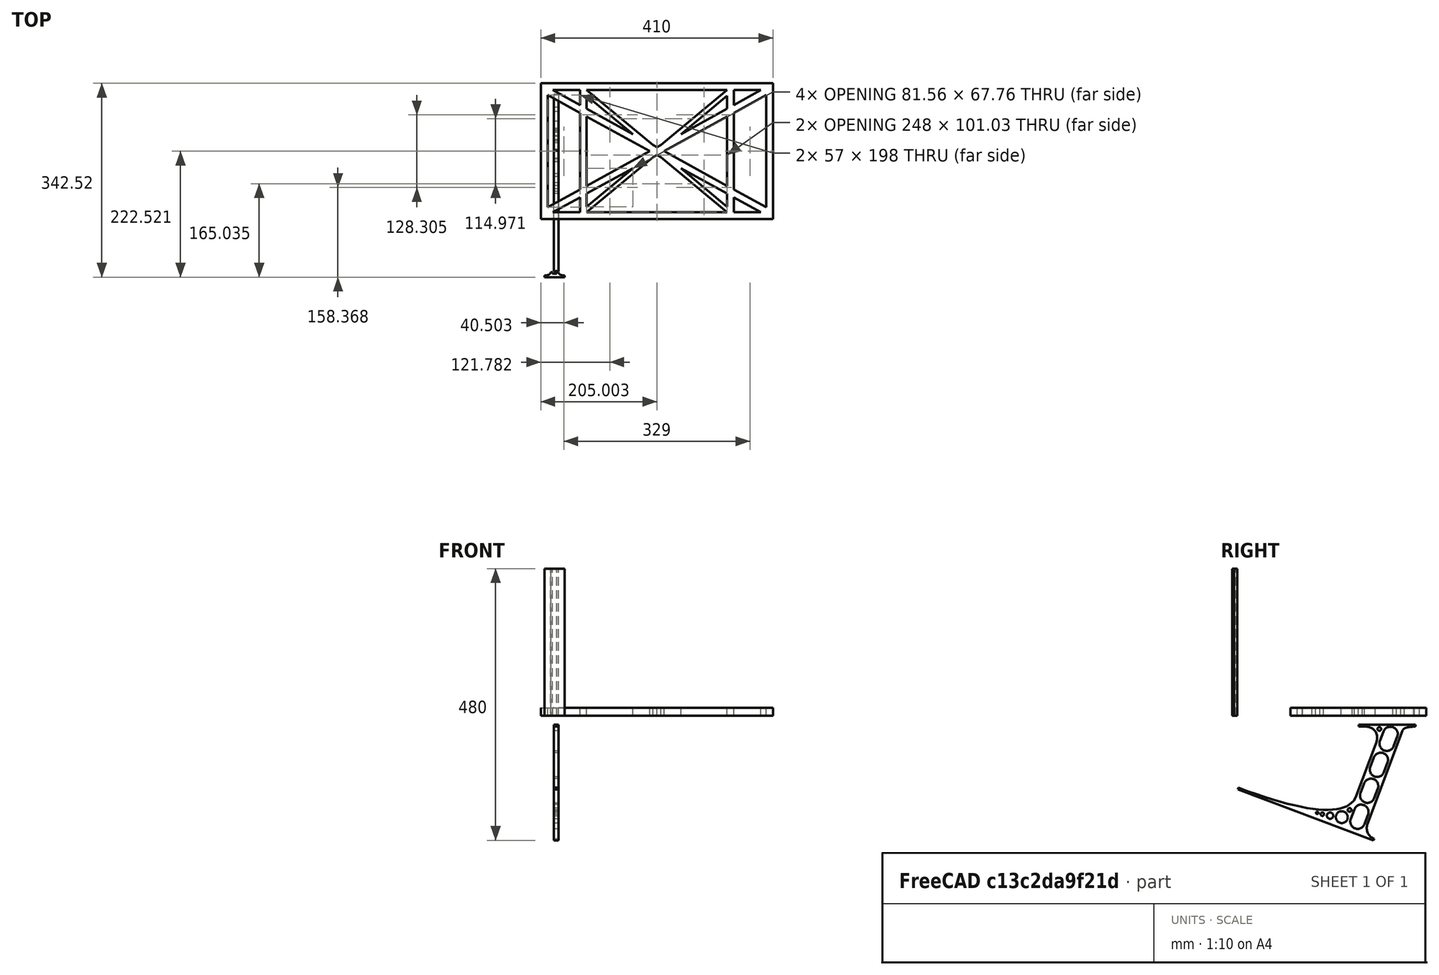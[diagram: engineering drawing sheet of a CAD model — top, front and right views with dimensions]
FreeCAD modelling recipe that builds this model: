
FCSTD DOCUMENT  (FreeCAD 0.19R0.19.2)
Label: laptopStand050
License: All rights reserved
LicenseURL: http://en.wikipedia.org/wiki/All_rights_reserved
objects: Sketcher::SketchObject×3, Part::Extrusion×3
note: 6 computed .brp shape members not serialized (recipe doc carries the construction recipe); baked Part::Feature solids carry a one-line shape summary decoded from their .brp

FEATURE [Sketcher::SketchObject] Sketch
  FullyConstrained = false
  sketch-geometry (72):
    g0: LineSegment StartX=-22.9272 StartY=136.221 StartZ=0 EndX=387.073 EndY=136.221 EndZ=0
    g1: LineSegment StartX=-22.9272 StartY=-103.779 StartZ=0 EndX=387.073 EndY=-103.779 EndZ=0
    g2: LineSegment StartX=375.073 StartY=115.221 StartZ=0 EndX=318.073 EndY=83.9235 EndZ=0
    g3: LineSegment StartX=-10.9272 StartY=-82.7794 StartZ=0 EndX=46.0728 EndY=-51.4823 EndZ=0
    g4: LineSegment StartX=-1.92719 StartY=124.221 StartZ=0 EndX=46.0728 EndY=97.8651 EndZ=0
    g5: LineSegment StartX=366.073 StartY=-91.7794 StartZ=0 EndX=318.073 EndY=-65.424 EndZ=0
    g6: LineSegment StartX=-10.9272 StartY=115.221 StartZ=0 EndX=-10.9272 EndY=-82.7794 EndZ=0
    g7: LineSegment StartX=375.073 StartY=-82.7794 StartZ=0 EndX=375.073 EndY=115.221 EndZ=0
    g8: LineSegment StartX=-1.92719 StartY=-91.7794 StartZ=0 EndX=46.0728 EndY=-91.7794 EndZ=0
    g9: LineSegment StartX=318.073 StartY=124.221 StartZ=0 EndX=366.073 EndY=124.221 EndZ=0
    g10: LineSegment StartX=306.073 StartY=-81.8102 StartZ=0 EndX=224.513 EndY=-14.0532 EndZ=0
    g11: LineSegment StartX=58.0728 StartY=114.251 StartZ=0 EndX=139.632 EndY=46.4944 EndZ=0
    g12: LineSegment StartX=306.073 StartY=124.221 StartZ=0 EndX=189.124 EndY=27.0628 EndZ=0
    g13: LineSegment StartX=58.0728 StartY=-91.7794 StartZ=0 EndX=175.022 EndY=5.37834 EndZ=0
    g14: LineSegment StartX=46.0728 StartY=124.221 StartZ=0 EndX=46.0728 EndY=97.8651 EndZ=0
    g15: LineSegment StartX=58.0728 StartY=-81.8102 StartZ=0 EndX=58.0728 EndY=-58.8351 EndZ=0
    g16: LineSegment StartX=318.073 StartY=124.221 StartZ=0 EndX=318.073 EndY=97.8651 EndZ=0
    g17: LineSegment StartX=306.073 StartY=114.251 StartZ=0 EndX=306.073 EndY=91.2763 EndZ=0
    g18: LineSegment StartX=224.513 StartY=46.4944 StartZ=0 EndX=306.073 EndY=114.251 EndZ=0
    g19: LineSegment StartX=175.022 StartY=27.0628 StartZ=0 EndX=58.0728 EndY=124.221 EndZ=0
    g20: LineSegment StartX=169.377 StartY=16.2206 StartZ=0 EndX=58.0728 EndY=77.3346 EndZ=0
    g21: LineSegment StartX=139.632 StartY=-14.0532 StartZ=0 EndX=58.0728 EndY=-81.8102 EndZ=0
    g22: LineSegment StartX=194.768 StartY=16.2206 StartZ=0 EndX=306.073 EndY=-44.8935 EndZ=0
    g23: LineSegment StartX=224.513 StartY=46.4944 StartZ=0 EndX=306.073 EndY=91.2763 EndZ=0
    g24: LineSegment StartX=175.022 StartY=27.0628 StartZ=0 EndX=179.022 EndY=24.8665 EndZ=0
    g25: LineSegment StartX=139.632 StartY=-14.0532 StartZ=0 EndX=58.0728 EndY=-58.8351 EndZ=0
    g26: LineSegment StartX=189.124 StartY=5.37834 StartZ=0 EndX=185.124 EndY=7.57463 EndZ=0
    g27: LineSegment StartX=189.124 StartY=5.37834 StartZ=0 EndX=306.073 EndY=-91.7794 EndZ=0
    g28: LineSegment StartX=306.073 StartY=77.3346 StartZ=0 EndX=306.073 EndY=-44.8935 EndZ=0
    g29: LineSegment StartX=318.073 StartY=83.9235 StartZ=0 EndX=318.073 EndY=-51.4823 EndZ=0
    g30: LineSegment StartX=318.073 StartY=97.8651 StartZ=0 EndX=366.073 EndY=124.221 EndZ=0
    g31: LineSegment StartX=306.073 StartY=77.3346 StartZ=0 EndX=194.768 EndY=16.2206 EndZ=0
    g32: LineSegment StartX=306.073 StartY=-58.8351 StartZ=0 EndX=224.513 EndY=-14.0532 EndZ=0
    g33: LineSegment StartX=306.073 StartY=-58.8351 StartZ=0 EndX=306.073 EndY=-81.8102 EndZ=0
    g34: LineSegment StartX=318.073 StartY=-51.4823 StartZ=0 EndX=375.073 EndY=-82.7794 EndZ=0
    g35: LineSegment StartX=318.073 StartY=-65.424 StartZ=0 EndX=318.073 EndY=-91.7794 EndZ=0
    g36: LineSegment StartX=318.073 StartY=-91.7794 StartZ=0 EndX=366.073 EndY=-91.7794 EndZ=0
    g37: LineSegment StartX=58.0728 StartY=-44.8935 StartZ=0 EndX=58.0728 EndY=77.3346 EndZ=0
    g38: LineSegment StartX=46.0728 StartY=-65.424 StartZ=0 EndX=-1.92719 EndY=-91.7794 EndZ=0
    g39: LineSegment StartX=46.0728 StartY=-65.424 StartZ=0 EndX=46.0728 EndY=-91.7794 EndZ=0
    g40: LineSegment StartX=58.0728 StartY=-44.8935 StartZ=0 EndX=169.377 EndY=16.2206 EndZ=0
    g41: LineSegment StartX=58.0728 StartY=91.2763 StartZ=0 EndX=58.0728 EndY=114.251 EndZ=0
    g42: LineSegment StartX=46.0728 StartY=83.9235 StartZ=0 EndX=46.0728 EndY=-51.4823 EndZ=0
    g43: LineSegment StartX=46.0728 StartY=124.221 StartZ=0 EndX=-1.92719 EndY=124.221 EndZ=0
    g44: LineSegment StartX=58.0728 StartY=91.2763 StartZ=0 EndX=139.632 EndY=46.4944 EndZ=0
    g45: LineSegment StartX=46.0728 StartY=83.9235 StartZ=0 EndX=-10.9272 EndY=115.221 EndZ=0
    g46: LineSegment StartX=-22.9272 StartY=136.221 StartZ=0 EndX=-42.9272 EndY=136.221 EndZ=0
    g47: LineSegment StartX=387.073 StartY=136.221 StartZ=0 EndX=407.073 EndY=136.221 EndZ=0
    g48: LineSegment StartX=-42.9272 StartY=136.221 StartZ=0 EndX=-42.9272 EndY=-103.779 EndZ=0
    g49: LineSegment StartX=-22.9272 StartY=-103.779 StartZ=0 EndX=-42.9272 EndY=-103.779 EndZ=0
    g50: LineSegment StartX=407.073 StartY=136.221 StartZ=0 EndX=407.073 EndY=-103.779 EndZ=0
    g51: LineSegment StartX=387.073 StartY=-103.779 StartZ=0 EndX=407.073 EndY=-103.779 EndZ=0
    g52: LineSegment StartX=179.022 StartY=27.0628 StartZ=0 EndX=179.022 EndY=124.221 EndZ=0
    g53: LineSegment StartX=185.124 StartY=27.0628 StartZ=0 EndX=185.124 EndY=124.221 EndZ=0
    g54: LineSegment StartX=179.022 StartY=27.0628 StartZ=0 EndX=179.022 EndY=24.8665 EndZ=0
    g55: LineSegment StartX=185.124 StartY=27.0628 StartZ=0 EndX=185.124 EndY=24.8665 EndZ=0
    g56: LineSegment StartX=185.124 StartY=7.57463 StartZ=0 EndX=185.124 EndY=-91.7794 EndZ=0
    g57: LineSegment StartX=179.022 StartY=7.57463 StartZ=0 EndX=179.022 EndY=-91.7794 EndZ=0
    g58: LineSegment StartX=189.124 StartY=27.0628 StartZ=0 EndX=185.124 EndY=24.8665 EndZ=0
    g59: LineSegment StartX=175.022 StartY=5.37834 StartZ=0 EndX=179.022 EndY=7.57463 EndZ=0
    g60: ArcOfCircle CenterX=-26.9272 CenterY=22.1087 CenterZ=0 NormalX=0 NormalY=0 NormalZ=1 AngleXU=0 Radius=8 StartAngle=1e-16 EndAngle=3.14159
    g61: ArcOfCircle CenterX=-26.9272 CenterY=-83.7794 CenterZ=0 NormalX=0 NormalY=0 NormalZ=1 AngleXU=0 Radius=8 StartAngle=3.14159 EndAngle=6.28319
    g62: LineSegment StartX=-34.9272 StartY=22.1087 StartZ=0 EndX=-34.9272 EndY=-83.7794 EndZ=0
    g63: LineSegment StartX=-18.9272 StartY=22.1087 StartZ=0 EndX=-18.9272 EndY=-83.7794 EndZ=0
    g64: LineSegment StartX=185.124 StartY=-91.7794 StartZ=0 EndX=306.073 EndY=-91.7794 EndZ=0
    g65: LineSegment StartX=179.022 StartY=-91.7794 StartZ=0 EndX=58.0728 EndY=-91.7794 EndZ=0
    g66: LineSegment StartX=306.073 StartY=124.221 StartZ=0 EndX=185.124 EndY=124.221 EndZ=0
    g67: LineSegment StartX=179.022 StartY=124.221 StartZ=0 EndX=58.0728 EndY=124.221 EndZ=0
    g68: ArcOfCircle CenterX=391.073 CenterY=22.1087 CenterZ=0 NormalX=0 NormalY=0 NormalZ=1 AngleXU=0 Radius=8 StartAngle=-4.4e-15 EndAngle=3.14159
    g69: LineSegment StartX=399.073 StartY=22.1087 StartZ=0 EndX=399.073 EndY=-83.7794 EndZ=0
    g70: LineSegment StartX=383.073 StartY=22.1087 StartZ=0 EndX=383.073 EndY=-83.7794 EndZ=0
    g71: ArcOfCircle CenterX=391.073 CenterY=-83.7794 CenterZ=0 NormalX=0 NormalY=0 NormalZ=1 AngleXU=0 Radius=8 StartAngle=3.14159 EndAngle=6.28319
  constraints (146):
    c: Horizontal(g0)
    c: Distance(g0) = 410
    c: Horizontal(g1)
    c: Block(g0)
    c: Horizontal(g8)
    c: Horizontal(g9)
    c: Tangent(g5,g20)
    c: PointOnObject(g20,g3)
    c: PointOnObject(g22,g2)
    c: Coincident(g44,g11)
    c: Coincident(g24,g19)
    c: Coincident(g18,g23)
    c: Coincident(g25,g21)
    c: Coincident(g32,g10)
    c: Coincident(g27,g26)
    c: Coincident(g18,g17)
    c: Tangent(g17,g28)
    c: Tangent(g16,g29)
    c: Coincident(g23,g17)
    c: Tangent(g23,g30)
    c: Coincident(g2,g29)
    c: Coincident(g31,g28)
    c: Tangent(g2,g31)
    c: Coincident(g33,g10)
    c: Tangent(g5,g32)
    c: Tangent(g28,g33)
    c: Coincident(g22,g28)
    c: Tangent(g22,g34)
    c: Coincident(g29,g34)
    c: Coincident(g35,g5)
    c: Tangent(g29,g35)
    c: Coincident(g21,g15)
    c: Tangent(g15,g37)
    c: Coincident(g25,g15)
    c: Tangent(g25,g38)
    c: Coincident(g39,g38)
    c: Tangent(g14,g39)
    c: Coincident(g3,g42)
    c: Coincident(g40,g37)
    c: Tangent(g3,g40)
    c: Tangent(g37,g41)
    c: Tangent(g14,g42)
    c: Coincident(g11,g41)
    c: Coincident(g4,g14)
    c: Coincident(g44,g41)
    c: Tangent(g4,g44)
    c: Coincident(g20,g37)
    c: Coincident(g45,g42)
    c: Tangent(g20,g45)
    c: Block(g19)
    c: Block(g12)
    c: Block(g16)
    c: Block(g30)
    c: Block(g2)
    c: Block(g34)
    c: Block(g7)
    c: Block(g32)
    c: Block(g33)
    c: Block(g5)
    c: Block(g35)
    c: Block(g18)
    c: Block(g27)
    c: Block(g13)
    c: Block(g25)
    c: Block(g21)
    c: Block(g39)
    c: Block(g38)
    c: Block(g3)
    c: Block(g6)
    c: Block(g45)
    c: Block(g4)
    c: Block(g14)
    c: Block(g11)
    c: Block(g41)
    c: Block(g31)
    c: Block(g28)
    c: Block(g20)
    c: Block(g40)
    c: Block(g43)
    c: Block(g9)
    c: Block(g36)
    c: Block(g8)
    c: Horizontal(g46)
    c: Distance(g46) = 20
    c: Coincident(g47,g0)
    c: Horizontal(g47)
    c: Distance(g47) = 20
    c: Coincident(g48,g46)
    c: Vertical(g48)
    c: Horizontal(g49)
    c: Coincident(g49,g48)
    c: Coincident(g50,g47)
    c: Vertical(g50)
    c: Coincident(g51,g1)
    c: Horizontal(g51)
    c: Coincident(g51,g50)
    c: Block(g50)
    c: Block(g49)
    c: Block(g48)
    c: Block(g1)
    c: Vertical(g52)
    c: Vertical(g53)
    c: Vertical(g54)
    c: Vertical(g55)
    c: Tangent(g55,g56)
    c: Tangent(g54,g57)
    c: Coincident(g24,g54)
    c: Coincident(g26,g56)
    c: Block(g52)
    c: Block(g53)
    c: Block(g57)
    c: Block(g56)
    c: Coincident(g58,g12)
    c: Coincident(g58,g55)
    c: Coincident(g59,g13)
    c: Coincident(g59,g57)
    c: Tangent(g60,g63) = 1.5708
    c: Tangent(g60,g62) = -1.5708
    c: Tangent(g62,g61) = -1.5708
    c: Tangent(g63,g61) = 1.5708
    c: Vertical(g62)
    c: Equal(g60,g61)
    c: Block(g63)
    c: Block(g62)
    c: Coincident(g64,g56)
    c: Coincident(g64,g27)
    c: Horizontal(g64)
    c: Coincident(g65,g57)
    c: Coincident(g65,g13)
    c: Horizontal(g65)
    c: Coincident(g66,g12)
    c: Coincident(g66,g53)
    c: Horizontal(g66)
    c: Coincident(g67,g52)
    c: Coincident(g67,g19)
    c: Horizontal(g67)
    c: Distance(g51) = 20
    c: Distance(g1) = 410
    c: Tangent(g68,g69) = 1.5708
    c: Tangent(g69,g71) = 1.5708
    c: Equal(g68,g71)
    c: Coincident(g70,g68)
    c: Coincident(g70,g71)
    c: Vertical(g70)
    c: Block(g69)
    c: Block(g70)
FEATURE [Sketcher::SketchObject] Sketch001
  FullyConstrained = true
  MapMode = 4
  Placement = pos=(0,0,0) rot=(0.57735,0.57735,0.57735;2.0944rad)
  Support = -> [Sketch]
  sketch-geometry (46):
    g0: BSplineCurve PolesCount=3 KnotsCount=2 Degree=2 IsPeriodic=0
    g1: ArcOfCircle CenterX=73.122 CenterY=-32.2909 CenterZ=0 NormalX=0 NormalY=0 NormalZ=1 AngleXU=0 Radius=13 StartAngle=5.92268 EndAngle=9.06428
    g2: ArcOfCircle CenterX=66.7816 CenterY=-49.1439 CenterZ=0 NormalX=0 NormalY=0 NormalZ=1 AngleXU=0 Radius=13 StartAngle=2.78068 EndAngle=5.92131
    g3: ArcOfCircle CenterX=55.9263 CenterY=-78.1807 CenterZ=0 NormalX=0 NormalY=0 NormalZ=1 AngleXU=0 Radius=13 StartAngle=5.92268 EndAngle=9.06428
    g4: ArcOfCircle CenterX=49.5884 CenterY=-95.0342 CenterZ=0 NormalX=0 NormalY=0 NormalZ=1 AngleXU=0 Radius=13 StartAngle=2.78068 EndAngle=5.92131
    g5: ArcOfCircle CenterX=38.7206 CenterY=-124.067 CenterZ=0 NormalX=0 NormalY=0 NormalZ=1 AngleXU=0 Radius=13 StartAngle=5.92268 EndAngle=9.06428
    g6: ArcOfCircle CenterX=32.3875 CenterY=-140.92 CenterZ=0 NormalX=0 NormalY=0 NormalZ=1 AngleXU=0 Radius=13 StartAngle=2.78068 EndAngle=5.92131
    g7: ArcOfCircle CenterX=21.4715 CenterY=-169.934 CenterZ=0 NormalX=0 NormalY=0 NormalZ=1 AngleXU=0 Radius=13 StartAngle=5.92268 EndAngle=9.06428
    g8: ArcOfCircle CenterX=15.1336 CenterY=-186.787 CenterZ=0 NormalX=0 NormalY=0 NormalZ=1 AngleXU=0 Radius=13 StartAngle=2.78068 EndAngle=5.92131
    g9-g12: Circle x4 (B-spline internal-alignment scaffolding for g13; pole/knot coordinates omitted)
    g13: BSplineCurve PolesCount=4 KnotsCount=2 Degree=3 IsPeriodic=0
    g14: GeomPoint X=28.8094 Y=-19.0875 Z=0
    g15: GeomPoint X=47.0443 Y=-50.4712 Z=0
    g16: Circle CenterX=53.5586 CenterY=-23.2695 CenterZ=0 NormalX=0 NormalY=0 NormalZ=1 AngleXU=0 Radius=3.24518
    g17: Circle CenterX=-195.441 CenterY=-127.082 CenterZ=0 NormalX=0 NormalY=0 NormalZ=1 AngleXU=0 Radius=1
    g18: Circle CenterX=-8.24091 CenterY=-197.481 CenterZ=0 NormalX=0 NormalY=0 NormalZ=1 AngleXU=0 Radius=1
    g19: Circle CenterX=12.8789 CenterY=-141.321 CenterZ=0 NormalX=0 NormalY=0 NormalZ=1 AngleXU=0 Radius=1
    g20: BSplineCurve PolesCount=3 KnotsCount=2 Degree=2 IsPeriodic=0
    g21: GeomPoint X=-195.441 Y=-127.082 Z=0
    g22: GeomPoint X=12.8789 Y=-141.321 Z=0
    g23: Circle CenterX=-12.8016 CenterY=-179.036 CenterZ=0 NormalX=0 NormalY=0 NormalZ=1 AngleXU=0 Radius=10.5072
    g24: Circle CenterX=0.933922 CenterY=-166.43 CenterZ=0 NormalX=0 NormalY=0 NormalZ=1 AngleXU=0 Radius=3.26661
    g25: Circle CenterX=-33.5518 CenterY=-176.44 CenterZ=0 NormalX=0 NormalY=0 NormalZ=1 AngleXU=0 Radius=5.64388
    g26: Circle CenterX=-47.2366 CenterY=-173.859 CenterZ=0 NormalX=0 NormalY=0 NormalZ=1 AngleXU=0 Radius=3.01653
    g27: Circle CenterX=-56.2595 CenterY=-171.456 CenterZ=0 NormalX=0 NormalY=0 NormalZ=1 AngleXU=0 Radius=2.12826
    g28: ArcOfCircle CenterX=51.2151 CenterY=-198.473 CenterZ=0 NormalX=0 NormalY=0 NormalZ=1 AngleXU=0 Radius=20 StartAngle=2.78189 EndAngle=4.35269
    g29: LineSegment StartX=32.4951 StartY=-191.433 StartZ=0 EndX=94.6577 EndY=-26.1351 EndZ=0
    g30: LineSegment StartX=43.1192 StartY=-220.001 StartZ=0 EndX=-196.497 EndY=-129.89 EndZ=0
    g31: LineSegment StartX=43.1192 StartY=-220.001 StartZ=0 EndX=44.1752 EndY=-217.193 EndZ=0
    g32: LineSegment StartX=117.223 StartY=-19.0875 StartZ=0 EndX=117.223 EndY=-16.0875 EndZ=0
    g33: LineSegment StartX=117.223 StartY=-16.0875 StartZ=0 EndX=17.2232 EndY=-16.0875 EndZ=0
    g34: LineSegment StartX=17.2232 StartY=-16.0875 StartZ=0 EndX=17.2232 EndY=-19.0875 EndZ=0
    g35: LineSegment StartX=28.8094 StartY=-19.0875 StartZ=0 EndX=17.2232 EndY=-19.0875 EndZ=0
    g36: LineSegment StartX=47.0443 StartY=-50.4712 StartZ=0 EndX=12.8789 EndY=-141.321 EndZ=0
    g37: LineSegment StartX=-195.441 StartY=-127.082 StartZ=0 EndX=-196.497 EndY=-129.89 EndZ=0
    g38: LineSegment StartX=85.2864 StartY=-36.8765 StartZ=0 EndX=78.9396 EndY=-53.7463 EndZ=0
    g39: LineSegment StartX=60.9577 StartY=-27.7052 StartZ=0 EndX=54.6191 EndY=-44.5532 EndZ=0
    g40: LineSegment StartX=68.0907 StartY=-82.7664 StartZ=0 EndX=61.7465 EndY=-99.6365 EndZ=0
    g41: LineSegment StartX=43.7619 StartY=-73.595 StartZ=0 EndX=37.426 EndY=-90.4435 EndZ=0
    g42: LineSegment StartX=50.885 StartY=-128.652 StartZ=0 EndX=44.5456 EndY=-145.522 EndZ=0
    g43: LineSegment StartX=26.5562 StartY=-119.481 StartZ=0 EndX=20.2251 EndY=-136.329 EndZ=0
    g44: LineSegment StartX=9.3071 StartY=-165.349 StartZ=0 EndX=2.97115 EndY=-182.197 EndZ=0
    g45: LineSegment StartX=33.6358 StartY=-174.52 StartZ=0 EndX=27.2917 EndY=-191.39 EndZ=0
  constraints (70):
    c: Block(g0)
    c: Block(g1)
    c: Block(g2)
    c: Block(g4)
    c: Block(g3)
    c: Block(g6)
    c: Block(g5)
    c: Block(g8)
    c: Block(g7)
    c: Weight(g9) = 1
    c: Equal(g9,g10)
    c: Equal(g9,g11)
    c: Equal(g9,g12)
    c: InternalAlignment(g9-g12 -> g13) x4
    c: InternalAlignment(g14,g13)
    c: InternalAlignment(g15,g13)
    c: Block(g16)
    c: Weight(g17) = 1
    c: Equal(g17,g18)
    c: Equal(g17,g19)
    c: InternalAlignment(g17,g20)
    c: InternalAlignment(g18,g20)
    c: InternalAlignment(g19,g20)
    c: InternalAlignment(g21,g20)
    c: InternalAlignment(g22,g20)
    c: Block(g20)
    c: Block(g23)
    c: Block(g24)
    c: Block(g25)
    c: Block(g26)
    c: Block(g27)
    c: Block(g28)
    c: Coincident(g29,g28)
    c: Coincident(g29,g0)
    c: Block(g13)
    c: Coincident(g31,g30)
    c: Coincident(g31,g28)
    c: Block(g31)
    c: Coincident(g32,g0)
    c: Vertical(g32)
    c: Coincident(g33,g32)
    c: Horizontal(g33)
    c: Coincident(g34,g33)
    c: Vertical(g34)
    c: Block(g33)
    c: Coincident(g35,g13)
    c: Coincident(g35,g34)
    c: Horizontal(g35)
    c: Coincident(g36,g13)
    c: Coincident(g36,g20)
    c: Coincident(g37,g20)
    c: Coincident(g37,g30)
    c: Block(g30)
    c: Coincident(g38,g1)
    c: Coincident(g38,g2)
    c: Coincident(g39,g1)
    c: Coincident(g39,g2)
    c: Coincident(g40,g3)
    c: Coincident(g40,g4)
    c: Coincident(g41,g3)
    c: Coincident(g41,g4)
    c: Coincident(g42,g5)
    c: Coincident(g42,g6)
    c: Coincident(g43,g5)
    c: Coincident(g43,g6)
    c: Coincident(g44,g7)
    c: Coincident(g44,g8)
    c: Coincident(g45,g7)
    c: Coincident(g45,g8)
    c: Distance(g30) = 256
FEATURE [Part::Extrusion] Extrude002
  Base = -> Sketch001
  Dir = (1,0,0)
  DirMode = 2
  FaceMakerClass = Part::FaceMakerBullseye
  LengthFwd = 8
  LengthRev = 0
  Solid = true
  Symmetric = false
FEATURE [Sketcher::SketchObject] Sketch002
  FullyConstrained = true
  sketch-geometry (20):
    g0: LineSegment StartX=-2.77179 StartY=-200.304 StartZ=0 EndX=5.22821 EndY=-200.304 EndZ=0
    g1: LineSegment StartX=5.22821 StartY=-200.304 StartZ=0 EndX=5.22821 EndY=-197.304 EndZ=0
    g2: LineSegment StartX=-2.77179 StartY=-200.304 StartZ=0 EndX=-2.77179 EndY=-197.304 EndZ=0
    g3: LineSegment StartX=5.22821 StartY=-197.304 StartZ=0 EndX=8.22821 EndY=-197.304 EndZ=0
    g4: LineSegment StartX=-2.77179 StartY=-197.304 StartZ=0 EndX=-5.77179 EndY=-197.304 EndZ=0
    g5: LineSegment StartX=19.2282 StartY=-203.304 StartZ=0 EndX=19.2282 EndY=-206.304 EndZ=0
    g6: LineSegment StartX=-16.7718 StartY=-203.304 StartZ=0 EndX=-16.7718 EndY=-206.304 EndZ=0
    g7: LineSegment StartX=-16.7718 StartY=-206.304 StartZ=0 EndX=19.2282 EndY=-206.304 EndZ=0
    g8: Circle CenterX=-16.7718 CenterY=-203.304 CenterZ=0 NormalX=0 NormalY=0 NormalZ=1 AngleXU=0 Radius=1
    g9: Circle CenterX=-5.77179 CenterY=-203.304 CenterZ=0 NormalX=0 NormalY=0 NormalZ=1 AngleXU=0 Radius=1
    g10: Circle CenterX=-5.77179 CenterY=-197.304 CenterZ=0 NormalX=0 NormalY=0 NormalZ=1 AngleXU=0 Radius=1
    g11: BSplineCurve PolesCount=3 KnotsCount=2 Degree=2 IsPeriodic=0
    g12: GeomPoint X=-16.7718 Y=-203.304 Z=0
    g13: GeomPoint X=-5.77179 Y=-197.304 Z=0
    g14: Circle CenterX=19.2282 CenterY=-203.304 CenterZ=0 NormalX=0 NormalY=0 NormalZ=1 AngleXU=0 Radius=1
    g15: Circle CenterX=8.22821 CenterY=-203.304 CenterZ=0 NormalX=0 NormalY=0 NormalZ=1 AngleXU=0 Radius=1
    g16: Circle CenterX=8.22821 CenterY=-197.304 CenterZ=0 NormalX=0 NormalY=0 NormalZ=1 AngleXU=0 Radius=1
    g17: BSplineCurve PolesCount=3 KnotsCount=2 Degree=2 IsPeriodic=0
    g18: GeomPoint X=19.2282 Y=-203.304 Z=0
    g19: GeomPoint X=8.22821 Y=-197.304 Z=0
  constraints (41):
    c: Horizontal(g0)
    c: Distance(g0) = 8
    c: Coincident(g1,g0)
    c: Vertical(g1)
    c: Distance(g1) = 3
    c: Coincident(g2,g0)
    c: Vertical(g2)
    c: Distance(g2) = 3
    c: Coincident(g3,g1)
    c: Horizontal(g3)
    c: Distance(g3) = 3
    c: Coincident(g4,g2)
    c: Horizontal(g4)
    c: Distance(g4) = 3
    c: Vertical(g5)
    c: Vertical(g6)
    c: Coincident(g7,g6)
    c: Coincident(g7,g5)
    c: Weight(g8) = 1
    c: Equal(g8,g9)
    c: Equal(g8,g10)
    c: Coincident(g11,g4)
    c: InternalAlignment(g8,g11)
    c: InternalAlignment(g9,g11)
    c: InternalAlignment(g10,g11)
    c: InternalAlignment(g12,g11)
    c: InternalAlignment(g13,g11)
    c: Coincident(g17,g5)
    c: Weight(g14) = 1
    c: Equal(g14,g15)
    c: Equal(g14,g16)
    c: Coincident(g17,g3)
    c: InternalAlignment(g14,g17)
    c: InternalAlignment(g15,g17)
    c: InternalAlignment(g16,g17)
    c: InternalAlignment(g18,g17)
    c: InternalAlignment(g19,g17)
    c: Block(g7)
    c: Block(g17)
    c: Block(g11)
    c: Block(g6)
FEATURE [Part::Extrusion] Extrude003
  Base = -> Sketch002
  Dir = (0,0,1)
  DirMode = 2
  FaceMakerClass = Part::FaceMakerBullseye
  LengthFwd = 260
  LengthRev = 0
  Solid = true
  Symmetric = false
FEATURE [Part::Extrusion] Extrude
  Base = -> Sketch
  Dir = (0,0,1)
  DirMode = 2
  FaceMakerClass = Part::FaceMakerBullseye
  LengthFwd = 14
  LengthRev = 0
  Solid = true
  Symmetric = false
